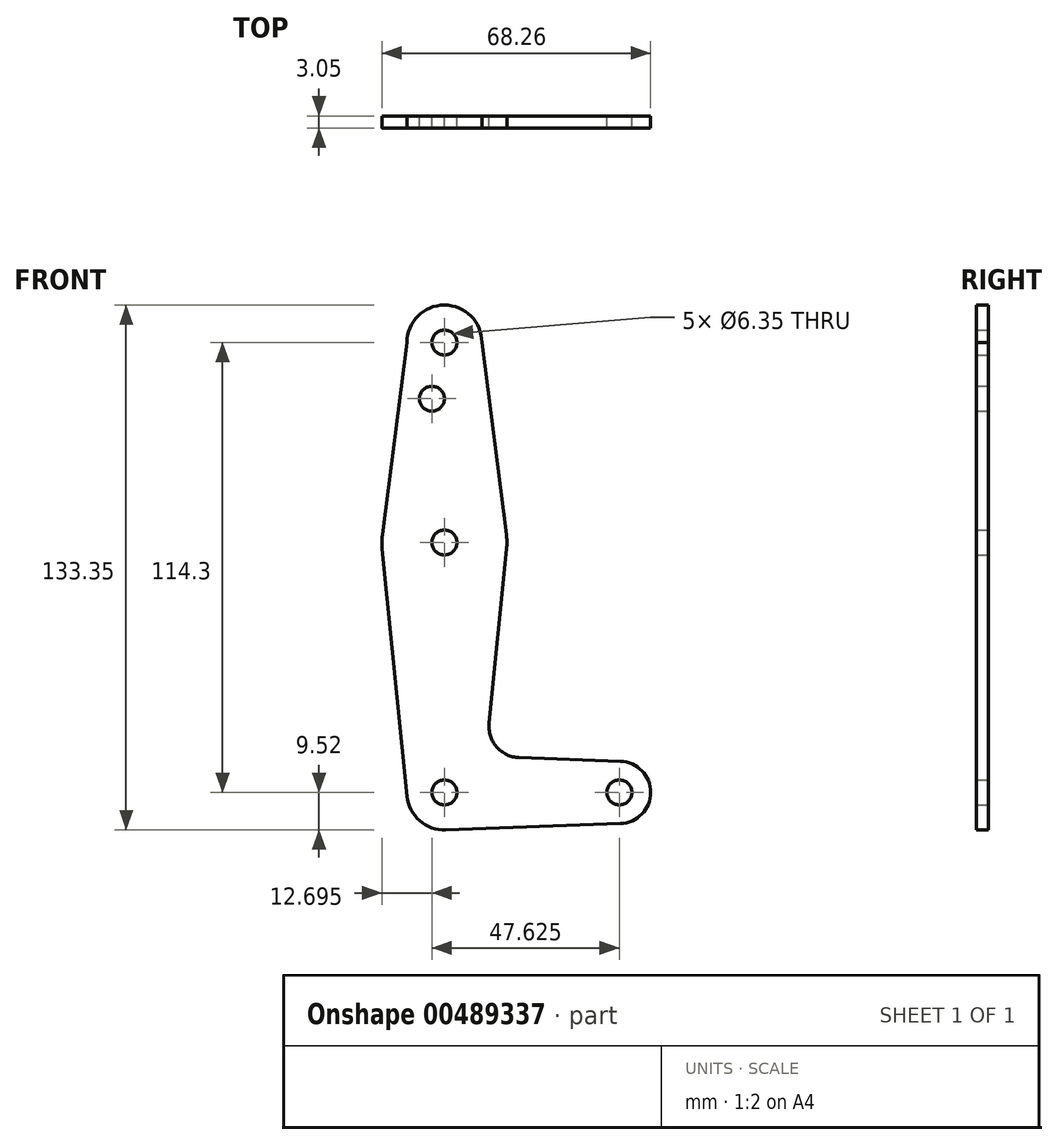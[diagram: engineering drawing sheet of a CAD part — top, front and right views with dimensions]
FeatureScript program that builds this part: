
annotation { "Feature Type Name" : "Feature", "Feature Type Description" : "" }
export const myFeature = defineFeature(function(context is Context, id is Id, definition is map)
    precondition{}
    {
        {
            var Q0;
            Q0=qCreatedBy(makeId("Front.planeOp"),FACE);
            var sketch = newSketch(context, id + "F0", { "sketchPlane" : qUnion([Q0])});
            skLineSegment(sketch, "E0", {"start": v(0, 0) * mm, "end": v(0, 114.3) * mm, "construction": true});
            skLineSegment(sketch, "E1", {"start": v(0, 0) * mm, "end": v(44.45, 0) * mm, "construction": true});
            skCircle(sketch, "E2", {"center": v(0, 0) * mm, "radius": 9.53 * mm});
            skCircle(sketch, "E3", {"center": v(44.45, 0) * mm, "radius": 7.94 * mm});
            skCircle(sketch, "E4", {"center": v(0, 114.3) * mm, "radius": 9.53 * mm});
            skCircle(sketch, "E5", {"center": v(0, 63.5) * mm, "radius": 15.88 * mm});
            skLineSegment(sketch, "E6", {"start": v(9.53, 114.3) * mm, "end": v(15.75, 65.5) * mm});
            skLineSegment(sketch, "E7", {"start": v(-9.53, 114.3) * mm, "end": v(-15.75, 65.5) * mm});
            skLineSegment(sketch, "E8", {"start": v(18.97, 8.85) * mm, "end": v(44.73, 7.93) * mm});
            skLineSegment(sketch, "E9", {"start": v(0.34, -9.52) * mm, "end": v(44.73, -7.93) * mm});
            skLineSegment(sketch, "E10", {"start": v(-15.8, 61.91) * mm, "end": v(-9.48, -0.95) * mm});
            skLineSegment(sketch, "E11", {"start": v(15.8, 61.91) * mm, "end": v(11.34, 17.6) * mm});
            skCircle(sketch, "E12", {"center": v(0, 114.3) * mm, "radius": 3.18 * mm});
            skCircle(sketch, "E13", {"center": v(0, 63.5) * mm, "radius": 3.18 * mm});
            skCircle(sketch, "E14", {"center": v(0, 0) * mm, "radius": 3.18 * mm});
            skCircle(sketch, "E15", {"center": v(44.45, 0) * mm, "radius": 3.18 * mm});
            skCircle(sketch, "E16", {"center": v(-3.18, 100.03) * mm, "radius": 3.18 * mm});
            skArc(sketch, "E17.filletArc", {"start": v(11.34, 17.6) * mm, "mid": v(13.26, 11.57) * mm, "end": v(18.97, 8.85) * mm});
            skSolve(sketch);
        }
        {
            var Q0;
            Q0=makeQuery(id+"F0.imprint","IMPRINT",FACE,{"disambiguationData":[TD([[makeQuery(id+"F0.imprint","IMPRINT",EDGE,{"derivedFrom":sQuery(id+"F0.wireOp",EDGE,"E14")}),-1.0]])]});
            var Q1;
            Q1=makeQuery(id+"F0.imprint","IMPRINT",FACE,{"disambiguationData":[TD([[makeQuery(id+"F0.imprint","IMPRINT",EDGE,{"derivedFrom":sQuery(id+"F0.wireOp",EDGE,"E15")}),-1.0]])]});
            var Q2;
            Q2=makeQuery(id+"F0.imprint","IMPRINT",FACE,{"disambiguationData":[TD([[makeQuery(id+"F0.imprint","IMPRINT",EDGE,{"derivedFrom":sQuery(id+"F0.wireOp",EDGE,"E12")}),-1.0]])]});
            var Q3;
            {var subQ3=sQuery(id+"F0.wireOp",EDGE,"E8");Q3=makeQuery(id+"F0.imprint","IMPRINT",FACE,{"disambiguationData":[TD([[makeQuery(id+"F0.imprint","IMPRINT",EDGE,{"derivedFrom":subQ3}),-1.0]])]});}
            var Q4;
            {var subQ1=sQuery(id+"F0.wireOp",EDGE,"E6");Q4=makeQuery(id+"F0.imprint","IMPRINT",FACE,{"disambiguationData":[TD([[makeQuery(id+"F0.imprint","IMPRINT",EDGE,{"derivedFrom":subQ1}),-1.0]])]});}
            var Q5;
            Q5=makeQuery(id+"F0.imprint","IMPRINT",FACE,{"disambiguationData":[TD([[makeQuery(id+"F0.imprint","IMPRINT",EDGE,{"derivedFrom":sQuery(id+"F0.wireOp",EDGE,"E13")}),-1.0]])]});
            extrude(context, id + "F1", {"entities" : qUnion([Q0, Q1, Q2, Q3, Q4, Q5]), "depth" : 3.05 * mm});
        }
        {
            var Q0;
            Q0 = qSketchRegion(id + "F0", true);
            extrude(context, id + "F2", {"entities" : qUnion([Q0]), "operationType" : NewBodyOperationType.ADD, "depth" : 3.05 * mm});
        }
    });
